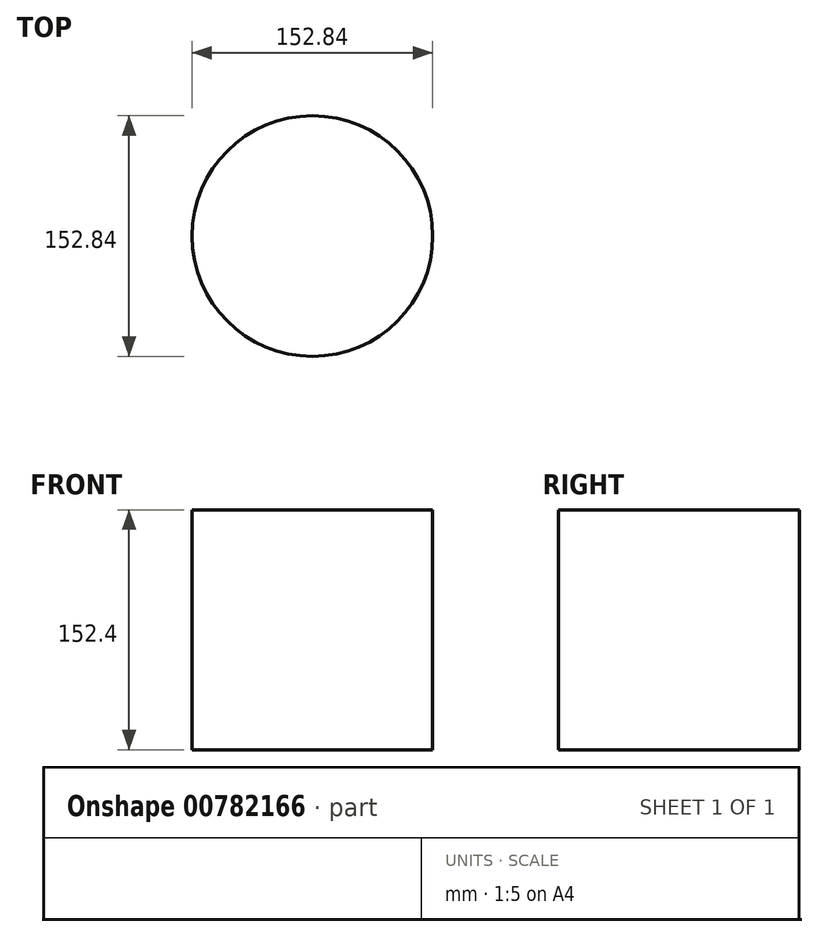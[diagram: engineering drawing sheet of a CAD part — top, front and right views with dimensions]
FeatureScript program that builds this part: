
annotation { "Feature Type Name" : "Feature", "Feature Type Description" : "" }
export const myFeature = defineFeature(function(context is Context, id is Id, definition is map)
    precondition{}
    {
        {
            var Q0;
            Q0=qCreatedBy(makeId("Top.planeOp"),FACE);
            var sketch = newSketch(context, id + "F0", { "sketchPlane" : qUnion([Q0])});
            skCircle(sketch, "E0", {"center": v(0, 0) * mm, "radius": 76.42 * mm});
            skSolve(sketch);
        }
        {
            var Q0;
            Q0=makeQuery(id+"F0.imprint","IMPRINT",FACE,{"disambiguationData":[TD([[makeQuery(id+"F0.imprint","IMPRINT",EDGE,{"derivedFrom":sQuery(id+"F0.wireOp",EDGE,"E0")}),1.0]])]});
            extrude(context, id + "F1", {"entities" : qUnion([Q0]), "depth" : 152.4 * mm, "offsetDistance" : 25.4 * mm});
        }
    });
